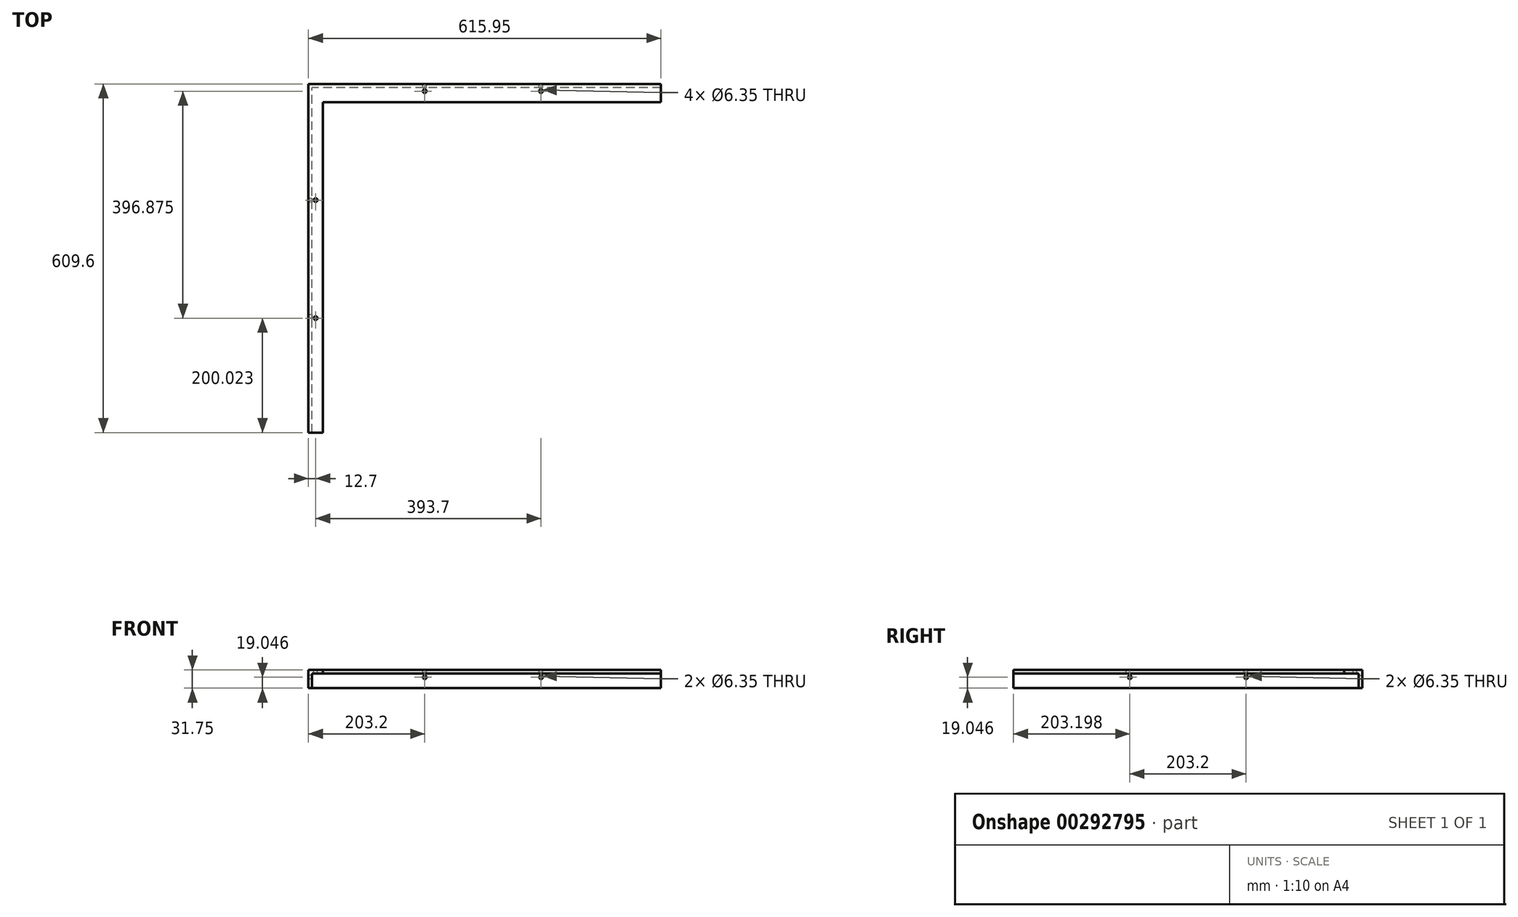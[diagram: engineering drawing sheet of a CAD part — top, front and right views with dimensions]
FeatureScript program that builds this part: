
annotation { "Feature Type Name" : "Feature", "Feature Type Description" : "" }
export const myFeature = defineFeature(function(context is Context, id is Id, definition is map)
    precondition{}
    {
        {
            var Q0;
            Q0=qCreatedBy(makeId("Right.planeOp"),FACE);
            var sketch = newSketch(context, id + "F0", { "sketchPlane" : qUnion([Q0])});
            skLineSegment(sketch, "E0.bottom", {"start": v(-46.8, 55.56) * mm, "end": v(562.8, 55.56) * mm});
            skLineSegment(sketch, "E0.top", {"start": v(-46.8, 61.9) * mm, "end": v(562.8, 61.9) * mm});
            skLineSegment(sketch, "E0.left", {"start": v(-46.8, 55.56) * mm, "end": v(-46.8, 61.9) * mm});
            skLineSegment(sketch, "E0.right", {"start": v(562.8, 55.56) * mm, "end": v(562.8, 61.9) * mm});
            skSolve(sketch);
        }
        {
            var Q0;
            Q0 = qSketchRegion(id + "F0", true);
            extrude(context, id + "F1", {"entities" : qUnion([Q0]), "depth" : 25.4 * mm});
        }
        {
            var Q0;
            Q0=makeQuery(id+"F1.opExtrude","SWEPT_FACE",FACE,{"disambiguationData":[OSD([sQuery(id+"F0.wireOp",EDGE,"E0.bottom")])]});
            var sketch = newSketch(context, id + "F2", { "sketchPlane" : qUnion([Q0])});
            skLineSegment(sketch, "E1.bottom", {"start": v(0, 46.8) * mm, "end": v(6.35, 46.8) * mm});
            skLineSegment(sketch, "E1.top", {"start": v(0, -562.8) * mm, "end": v(6.35, -562.8) * mm});
            skLineSegment(sketch, "E1.left", {"start": v(0, 46.8) * mm, "end": v(0, -562.8) * mm});
            skLineSegment(sketch, "E1.right", {"start": v(6.35, 46.8) * mm, "end": v(6.35, -562.8) * mm});
            skSolve(sketch);
        }
        {
            var Q0;
            Q0 = qSketchRegion(id + "F2", true);
            extrude(context, id + "F3", {"entities" : qUnion([Q0]), "operationType" : NewBodyOperationType.ADD, "depth" : 25.4 * mm});
        }
        {
            var Q0;
            Q0=makeQuery(id+"F3.opExtrude","SWEPT_FACE",FACE,{"disambiguationData":[OSD([sQuery(id+"F2.wireOp",EDGE,"E1.right")])]});
            var sketch = newSketch(context, id + "F4", { "sketchPlane" : qUnion([Q0])});
            skLineSegment(sketch, "E2.bottom", {"start": v(556.45, 61.9) * mm, "end": v(562.8, 61.9) * mm});
            skLineSegment(sketch, "E2.top", {"start": v(556.45, 30.16) * mm, "end": v(562.8, 30.16) * mm});
            skLineSegment(sketch, "E2.left", {"start": v(556.45, 61.9) * mm, "end": v(556.45, 30.16) * mm});
            skLineSegment(sketch, "E2.right", {"start": v(562.8, 61.9) * mm, "end": v(562.8, 30.16) * mm});
            skSolve(sketch);
        }
        {
            var Q0;
            Q0 = qSketchRegion(id + "F4", true);
            extrude(context, id + "F5", {"entities" : qUnion([Q0]), "operationType" : NewBodyOperationType.ADD, "depth" : 609.6 * mm});
        }
        {
            var Q0;
            Q0=makeQuery(id+"F1.opExtrude","CAP_FACE",FACE,{"disambiguationData":[OSD([sQuery(id+"F0.wireOp",EDGE,"E0.bottom"),sQuery(id+"F0.wireOp",EDGE,"E0.top"),sQuery(id+"F0.wireOp",EDGE,"E0.left"),sQuery(id+"F0.wireOp",EDGE,"E0.right")])],"isStart":false});
            var sketch = newSketch(context, id + "F6", { "sketchPlane" : qUnion([Q0])});
            skLineSegment(sketch, "E3.bottom", {"start": v(556.45, 61.9) * mm, "end": v(531.05, 61.9) * mm});
            skLineSegment(sketch, "E3.top", {"start": v(556.45, 55.56) * mm, "end": v(531.05, 55.56) * mm});
            skLineSegment(sketch, "E3.left", {"start": v(556.45, 61.9) * mm, "end": v(556.45, 55.56) * mm});
            skLineSegment(sketch, "E3.right", {"start": v(531.05, 61.9) * mm, "end": v(531.05, 55.56) * mm});
            skSolve(sketch);
        }
        {
            var Q0;
            Q0 = qSketchRegion(id + "F6", true);
            extrude(context, id + "F7", {"entities" : qUnion([Q0]), "operationType" : NewBodyOperationType.ADD, "depth" : 590.55 * mm});
        }
        {
            var Q0;
            Q0=makeQuery(id+"F7.boolean.opBoolean","MERGE",FACE,{"derivedFrom":[makeQuery(id+"F5.boolean.opBoolean","MERGE",FACE,{"derivedFrom":[makeQuery(id+"F1.opExtrude","SWEPT_FACE",FACE,{"disambiguationData":[OSD([sQuery(id+"F0.wireOp",EDGE,"E0.top")])]}),makeQuery(id+"F5.opExtrude","SWEPT_FACE",FACE,{"disambiguationData":[OSD([sQuery(id+"F4.wireOp",EDGE,"E2.bottom")])]})]}),makeQuery(id+"F7.opExtrude","SWEPT_FACE",FACE,{"disambiguationData":[OSD([sQuery(id+"F6.wireOp",EDGE,"E3.bottom")])]})]});
            var sketch = newSketch(context, id + "F8", { "sketchPlane" : qUnion([Q0])});
            skCircle(sketch, "E4", {"center": v(12.7, 153.22) * mm, "radius": 3.18 * mm});
            skCircle(sketch, "E5", {"center": v(12.7, 359.6) * mm, "radius": 3.12 * mm});
            skSolve(sketch);
        }
        {
            var Q0;
            Q0=makeQuery(id+"F8.imprint","IMPRINT",FACE,{"disambiguationData":[TD([[makeQuery(id+"F8.imprint","IMPRINT",EDGE,{"derivedFrom":sQuery(id+"F8.wireOp",EDGE,"E4")}),-1.0]])]});
            var sketch = newSketch(context, id + "F9", { "sketchPlane" : qUnion([Q0])});
            skCircle(sketch, "E6", {"center": v(203.2, 550.1) * mm, "radius": 3.18 * mm});
            skCircle(sketch, "E7", {"center": v(406.4, 550.1) * mm, "radius": 3.5 * mm});
            skSolve(sketch);
        }
        {
            var Q0;
            Q0=makeQuery(id+"F5.boolean.opBoolean","MERGE",FACE,{"derivedFrom":[makeQuery(id+"F3.boolean.opBoolean","MERGE",FACE,{"derivedFrom":[makeQuery(id+"F1.opExtrude","SWEPT_FACE",FACE,{"disambiguationData":[OSD([sQuery(id+"F0.wireOp",EDGE,"E0.right")])]}),makeQuery(id+"F3.opExtrude","SWEPT_FACE",FACE,{"disambiguationData":[OSD([sQuery(id+"F2.wireOp",EDGE,"E1.top")])]})]}),makeQuery(id+"F5.opExtrude","SWEPT_FACE",FACE,{"disambiguationData":[OSD([sQuery(id+"F4.wireOp",EDGE,"E2.right")])]})]});
            var sketch = newSketch(context, id + "F10", { "sketchPlane" : qUnion([Q0])});
            skCircle(sketch, "E8", {"center": v(-203.2, 49.2) * mm, "radius": 3.18 * mm});
            skCircle(sketch, "E9", {"center": v(-406.4, 49.2) * mm, "radius": 3.18 * mm});
            skSolve(sketch);
        }
        {
            var Q0;
            Q0=makeQuery(id+"F3.boolean.opBoolean","MERGE",FACE,{"derivedFrom":[makeQuery(id+"F1.opExtrude","CAP_FACE",FACE,{"disambiguationData":[OSD([sQuery(id+"F0.wireOp",EDGE,"E0.bottom"),sQuery(id+"F0.wireOp",EDGE,"E0.top"),sQuery(id+"F0.wireOp",EDGE,"E0.left"),sQuery(id+"F0.wireOp",EDGE,"E0.right")])],"isStart":true}),makeQuery(id+"F3.opExtrude","SWEPT_FACE",FACE,{"disambiguationData":[OSD([sQuery(id+"F2.wireOp",EDGE,"E1.left")])]})]});
            var sketch = newSketch(context, id + "F11", { "sketchPlane" : qUnion([Q0])});
            skCircle(sketch, "E10", {"center": v(-359.6, 49.2) * mm, "radius": 3.18 * mm});
            skCircle(sketch, "E11", {"center": v(-156.4, 49.2) * mm, "radius": 3.18 * mm});
            skSolve(sketch);
        }
        {
            var Q0;
            Q0=sQuery(id+"F8.wireOp",VERTEX,"E5.center");
            var Q1;
            Q1=sQuery(id+"F8.wireOp",VERTEX,"E4.center");
            var Q2;
            Q2=makeQuery(id+"F1.opExtrude","SWEPT_BODY",BODY,{"disambiguationData":[OSD([sQuery(id+"F0.wireOp",EDGE,"E0.bottom"),sQuery(id+"F0.wireOp",EDGE,"E0.top"),sQuery(id+"F0.wireOp",EDGE,"E0.left"),sQuery(id+"F0.wireOp",EDGE,"E0.right")])]});
            hole(context, id + "F12", {"style" : HoleStyle.SIMPLE, "endStyle" : HoleEndStyle.BLIND, "holeDiameter" : 6.35 * mm, "holeDepth" : 6.35 * mm, "tappedDepth" : 12.7 * mm, "tapClearance" : 3, "locations" : qUnion([Q0, Q1]), "scope" : qUnion([Q2])});
        }
        {
            var Q0;
            Q0=sQuery(id+"F11.wireOp",VERTEX,"E10.center");
            var Q1;
            Q1=sQuery(id+"F11.wireOp",VERTEX,"E11.center");
            var Q2;
            Q2=sQuery(id+"F10.wireOp",VERTEX,"E8.center");
            var Q3;
            Q3=sQuery(id+"F10.wireOp",VERTEX,"E9.center");
            var Q4;
            Q4=sQuery(id+"F9.wireOp",VERTEX,"E7.center");
            var Q5;
            Q5=sQuery(id+"F9.wireOp",VERTEX,"E6.center");
            var Q6;
            Q6=makeQuery(id+"F1.opExtrude","SWEPT_BODY",BODY,{"disambiguationData":[OSD([sQuery(id+"F0.wireOp",EDGE,"E0.bottom"),sQuery(id+"F0.wireOp",EDGE,"E0.top"),sQuery(id+"F0.wireOp",EDGE,"E0.left"),sQuery(id+"F0.wireOp",EDGE,"E0.right")])]});
            hole(context, id + "F13", {"style" : HoleStyle.SIMPLE, "endStyle" : HoleEndStyle.BLIND, "holeDiameter" : 6.35 * mm, "holeDepth" : 6.35 * mm, "tappedDepth" : 12.7 * mm, "tapClearance" : 3, "locations" : qUnion([Q0, Q1, Q2, Q3, Q4, Q5]), "scope" : qUnion([Q6])});
        }
    });
